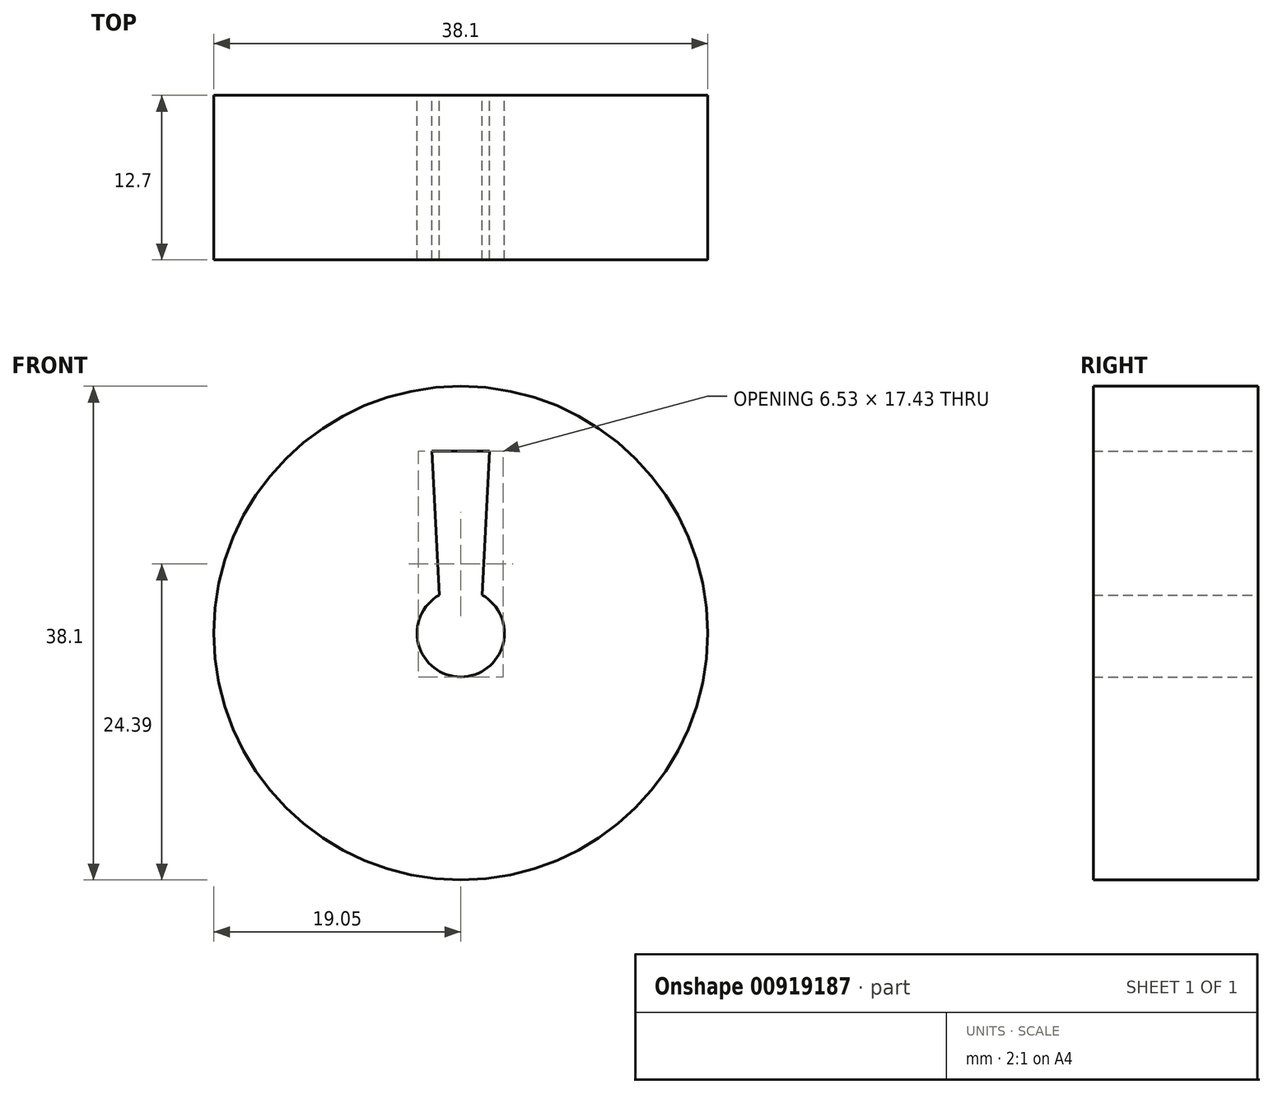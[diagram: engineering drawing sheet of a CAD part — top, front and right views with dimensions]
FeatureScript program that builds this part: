
annotation { "Feature Type Name" : "Feature", "Feature Type Description" : "" }
export const myFeature = defineFeature(function(context is Context, id is Id, definition is map)
    precondition{}
    {
        {
            var Q0;
            Q0=qCreatedBy(makeId("Front.planeOp"),FACE);
            var sketch = newSketch(context, id + "F0", { "sketchPlane" : qUnion([Q0])});
            skCircle(sketch, "E0", {"center": v(0, 0) * mm, "radius": 19.05 * mm});
            skArc(sketch, "E1", {"start": v(-1.65, 2.94) * mm, "mid": v(0, -3.37) * mm, "end": v(1.65, 2.94) * mm});
            skLineSegment(sketch, "E2", {"start": v(-1.65, 2.94) * mm, "end": v(-1.65, 14.05) * mm, "construction": true});
            skLineSegment(sketch, "E3", {"start": v(1.65, 14.05) * mm, "end": v(1.65, 2.94) * mm, "construction": true});
            skLineSegment(sketch, "E4", {"start": v(-1.65, 2.94) * mm, "end": v(-2.22, 14.05) * mm});
            skLineSegment(sketch, "E5", {"start": v(1.65, 2.94) * mm, "end": v(2.22, 14.05) * mm});
            skLineSegment(sketch, "E6", {"start": v(-2.22, 14.05) * mm, "end": v(2.22, 14.05) * mm});
            skLineSegment(sketch, "E7", {"start": v(0, 24.84) * mm, "end": v(0, -25.9) * mm, "construction": true});
            skLineSegment(sketch, "E8", {"start": v(-1.65, 2.94) * mm, "end": v(1.65, 2.94) * mm, "construction": true});
            skSolve(sketch);
        }
        {
            var Q0;
            Q0=makeQuery(id+"F0.imprint","IMPRINT",FACE,{"disambiguationData":[TD([[makeQuery(id+"F0.imprint","IMPRINT",EDGE,{"derivedFrom":sQuery(id+"F0.wireOp",EDGE,"E0")}),1.0]])]});
            extrude(context, id + "F1", {"entities" : qUnion([Q0]), "depth" : 12.7 * mm, "offsetDistance" : 25.4 * mm});
        }
    });
